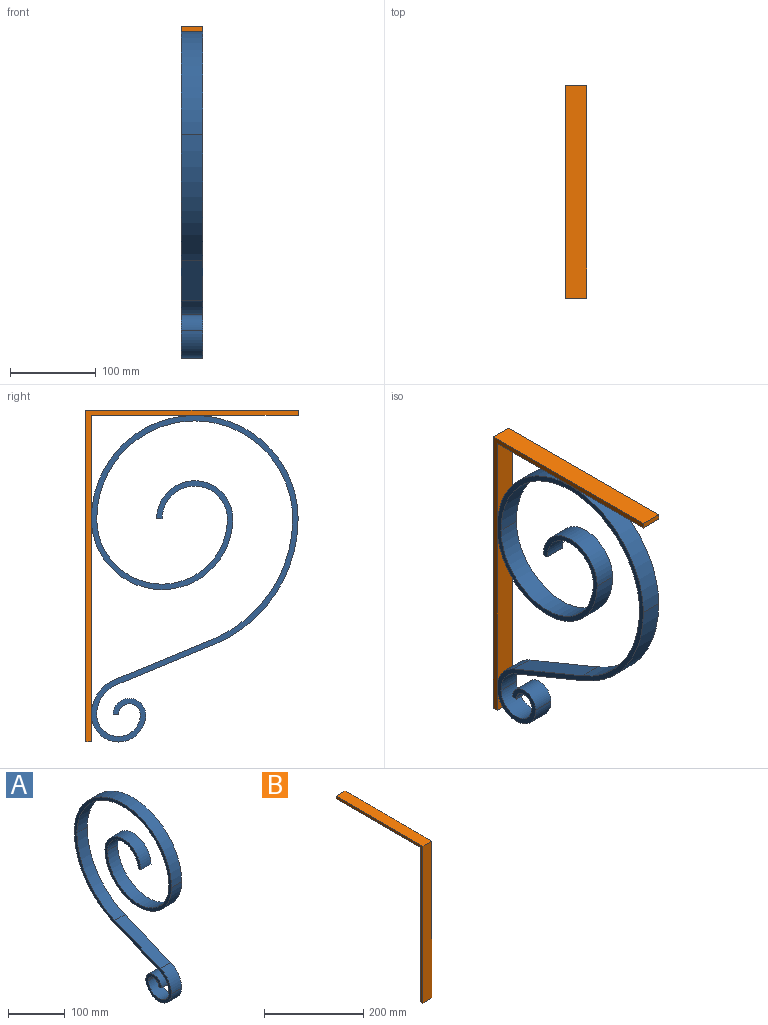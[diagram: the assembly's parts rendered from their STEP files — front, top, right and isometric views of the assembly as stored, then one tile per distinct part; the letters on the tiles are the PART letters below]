
ASSEMBLY  parts=2 mates=1
PART A: 20 faces, bbox 25.4x241.3x381 mm
  f0: cylinder r=76.2mm len=152.4mm, axis (-1,0,0), area 6080.5mm2, adj f1,f17,f18,f19
  f1: cylinder r=114.3mm len=228.6mm, axis (-1,0,0), area 9120.7mm2, adj f0,f2,f18,f19
  f2: cylinder r=152.4mm len=140.91mm, axis (-1,0,0), area 4567.7mm2, adj f1,f3,f18,f19
  f3: plane 113.09x46.59mm, normal (0,-0.38,0.92), area 3106.7mm2, adj f2,f4,f18,f19
  f4: cylinder r=44.45mm len=41.1mm, axis (-1,0,0), area 1332.2mm2, adj f3,f5,f18,f19
  f5: cylinder r=31.75mm len=63.5mm, axis (-1,0,0), area 2533.5mm2, adj f4,f6,f18,f19
  f6: cylinder r=19.05mm len=38.1mm, axis (-1,0,0), area 1520.1mm2, adj f5,f7,f18,f19
  f7: plane 25.4x6.35mm, normal (0,0,-1), area 161.3mm2, adj f6,f8,f18,f19
  f8: cylinder r=12.7mm len=25.4mm, axis (-1,0,0), area 1013.4mm2, adj f7,f9,f18,f19
  f9: cylinder r=25.4mm len=50.8mm, axis (-1,0,0), area 2026.8mm2, adj f8,f10,f18,f19
  f10: cylinder r=38.1mm len=35.23mm, axis (-1,0,0), area 1141.9mm2, adj f9,f11,f18,f19
  f11: plane 113.09x46.59mm, normal (0,0.38,-0.92), area 3106.7mm2, adj f10,f12,f18,f19
  f12: cylinder r=158.75mm len=146.78mm, axis (-1,0,0), area 4758mm2, adj f11,f13,f18,f19
  f13: cylinder r=120.65mm len=241.3mm, axis (-1,0,0), area 9627.4mm2, adj f12,f14,f18,f19
  f14: cylinder r=82.55mm len=165.1mm, axis (-1,0,0), area 6587.2mm2, adj f13,f15,f18,f19
  f15: cylinder r=44.45mm len=88.9mm, axis (-1,0,0), area 3547mm2, adj f14,f16,f18,f19
  f16: plane 25.4x6.35mm, normal (0,0,-1), area 161.3mm2, adj f15,f17,f18,f19
  f17: cylinder r=38.1mm len=76.2mm, axis (-1,0,0), area 3040.2mm2, adj f0,f16,f18,f19
  f18: plane 381x241.3mm, normal (1,0,0), area 7888.8mm2, adj f0,f1,f2,f3,f4,f5,f6,f7
  f19: plane 381x241.3mm, normal (-1,0,0), area 7888.8mm2, adj f0,f1,f2,f3,f4,f5,f6,f7
PART B: 8 faces, bbox 25.4x247.7x387.4 mm
  f0: plane 25.4x6.35mm, normal (0,0,-1), area 161.3mm2, adj f1,f5,f6,f7
  f1: plane 381x25.4mm, normal (0,1,0), area 9677.4mm2, adj f0,f2,f6,f7
  f2: plane 241.3x25.4mm, normal (0,0,-1), area 6129mm2, adj f1,f3,f6,f7
  f3: plane 25.4x6.35mm, normal (0,1,0), area 161.3mm2, adj f2,f4,f6,f7
  f4: plane 247.65x25.4mm, normal (0,0,1), area 6290.3mm2, adj f3,f5,f6,f7
  f5: plane 387.35x25.4mm, normal (0,-1,0), area 9838.7mm2, adj f0,f4,f6,f7
  f6: plane 387.35x247.65mm, normal (1,0,0), area 3991.9mm2, adj f0,f1,f2,f3,f4,f5
  f7: plane 387.35x247.65mm, normal (-1,0,0), area 3991.9mm2, adj f0,f1,f2,f3,f4,f5
PLACE A rot(axis=(0,0,-1),180deg) t=(-136.98,256.34,-74.25)mm
PLACE B rot(axis=(0,0,-1),180deg) t=(-136.98,294.44,-106)mm
MATE planar B.f6 <-> A.f18  axis (-1,0,0) through (-162.38,167.44,275)mm
